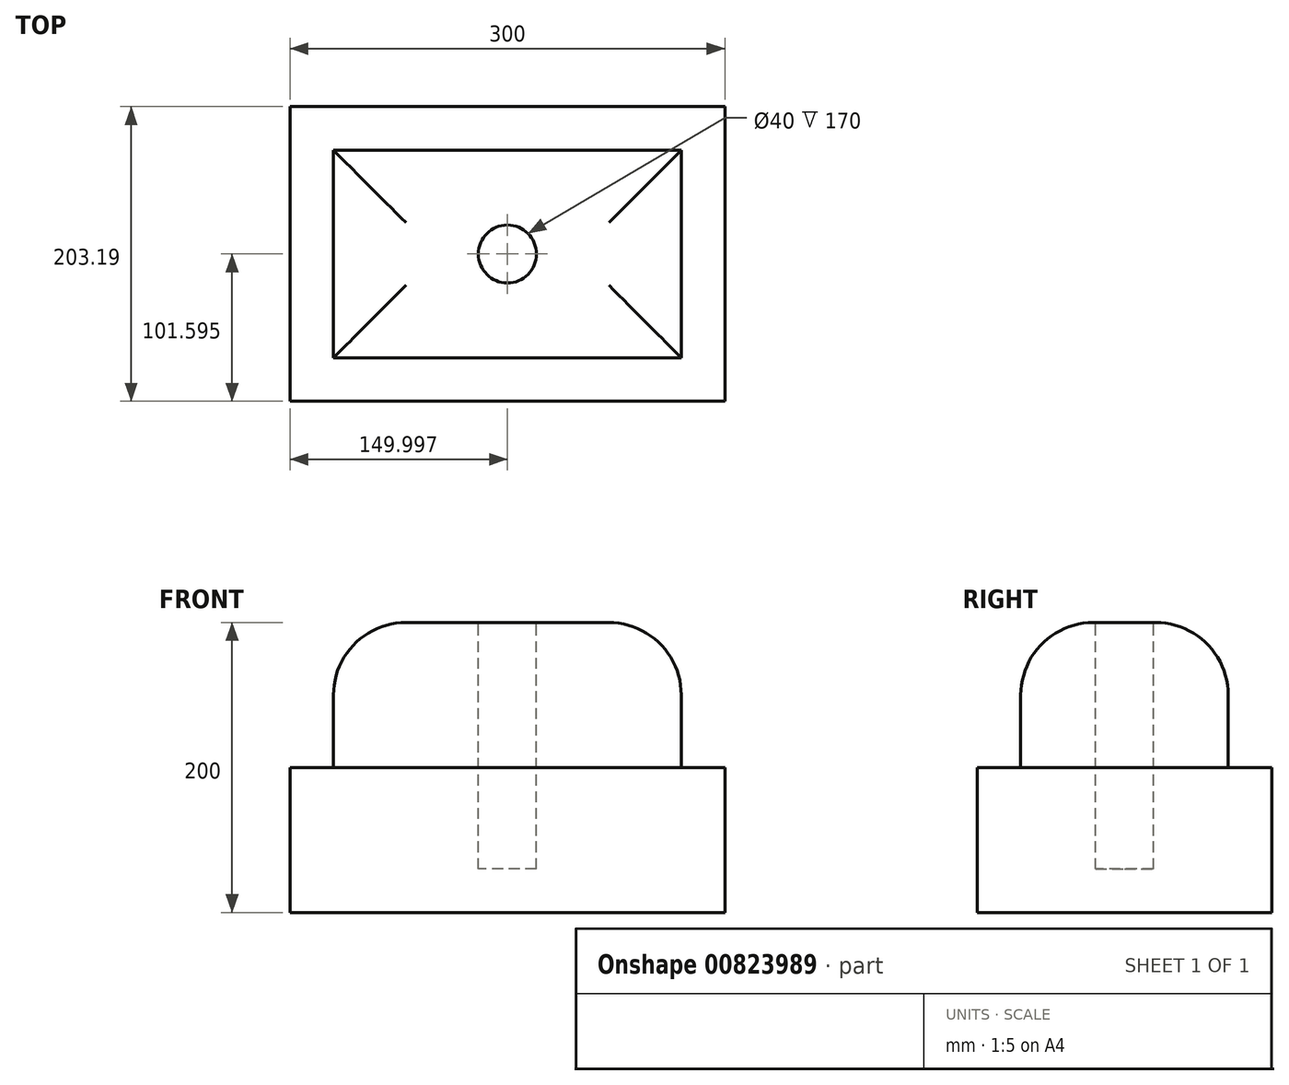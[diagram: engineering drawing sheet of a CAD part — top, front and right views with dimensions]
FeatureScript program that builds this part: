
annotation { "Feature Type Name" : "Feature", "Feature Type Description" : "" }
export const myFeature = defineFeature(function(context is Context, id is Id, definition is map)
    precondition{}
    {
        {
            var Q0;
            Q0=qCreatedBy(makeId("Top.planeOp"),FACE);
            var sketch = newSketch(context, id + "F0", { "sketchPlane" : qUnion([Q0])});
            skLineSegment(sketch, "E0", {"start": v(-72.68, 128.13) * mm, "end": v(227.32, 128.13) * mm});
            skLineSegment(sketch, "E1", {"start": v(-72.68, 128.13) * mm, "end": v(-72.68, -75.06) * mm});
            skLineSegment(sketch, "E2", {"start": v(-72.68, -75.06) * mm, "end": v(227.32, -75.06) * mm});
            skLineSegment(sketch, "E3", {"start": v(227.32, -75.06) * mm, "end": v(227.32, 128.13) * mm});
            skSolve(sketch);
        }
        {
            var Q0;
            Q0=makeQuery(id+"F0.imprint","IMPRINT",FACE,{"disambiguationData":[TD([[makeQuery(id+"F0.imprint","IMPRINT",EDGE,{"derivedFrom":sQuery(id+"F0.wireOp",EDGE,"E0")}),-1.0]])]});
            extrude(context, id + "F1", {"entities" : qUnion([Q0]), "depth" : 100 * mm, "offsetDistance" : 25 * mm});
        }
        {
            var Q0;
            Q0=makeQuery(id+"F1.opExtrude","CAP_FACE",FACE,{"disambiguationData":[OSD([sQuery(id+"F0.wireOp",EDGE,"E0"),sQuery(id+"F0.wireOp",EDGE,"E1"),sQuery(id+"F0.wireOp",EDGE,"E2"),sQuery(id+"F0.wireOp",EDGE,"E3")])],"isStart":false});
            var sketch = newSketch(context, id + "F2", { "sketchPlane" : qUnion([Q0])});
            skLineSegment(sketch, "E4", {"start": v(-42.68, 98.13) * mm, "end": v(197.32, 98.13) * mm});
            skLineSegment(sketch, "E5.MirrorCS", {"start": v(-42.68, -45.06) * mm, "end": v(197.32, -45.06) * mm});
            skLineSegment(sketch, "E6", {"start": v(-42.68, 98.13) * mm, "end": v(-42.68, -45.06) * mm});
            skLineSegment(sketch, "E7", {"start": v(197.32, 98.13) * mm, "end": v(197.32, -45.06) * mm});
            skSolve(sketch);
        }
        {
            var Q0;
            Q0 = qSketchRegion(id + "F2", true);
            extrude(context, id + "F3", {"entities" : qUnion([Q0]), "operationType" : NewBodyOperationType.ADD, "depth" : 100 * mm, "offsetDistance" : 25 * mm});
        }
        {
            var Q0;
            Q0=makeQuery(id+"F3.opExtrude","CAP_EDGE",EDGE,{"disambiguationData":[OSD([sQuery(id+"F2.wireOp",EDGE,"E4")])],"isStart":false});
            var Q1;
            Q1=makeQuery(id+"F3.opExtrude","CAP_EDGE",EDGE,{"disambiguationData":[OSD([sQuery(id+"F2.wireOp",EDGE,"E6")])],"isStart":false});
            var Q2;
            Q2=makeQuery(id+"F3.opExtrude","CAP_EDGE",EDGE,{"disambiguationData":[OSD([sQuery(id+"F2.wireOp",EDGE,"E5.MirrorCS")])],"isStart":false});
            var Q3;
            Q3=makeQuery(id+"F3.opExtrude","CAP_EDGE",EDGE,{"disambiguationData":[OSD([sQuery(id+"F2.wireOp",EDGE,"E7")])],"isStart":false});
            fillet(context, id + "F4", {"entities" : qUnion([Q0, Q1, Q2, Q3]), "radius" : 50 * mm, "tangentPropagation" : true, "allowEdgeOverflow" : false});
        }
        {
            var Q0;
            Q0=makeQuery(id+"F3.opExtrude","CAP_FACE",FACE,{"disambiguationData":[OSD([sQuery(id+"F2.wireOp",EDGE,"E4"),sQuery(id+"F2.wireOp",EDGE,"E5.MirrorCS"),sQuery(id+"F2.wireOp",EDGE,"E6"),sQuery(id+"F2.wireOp",EDGE,"E7")])],"isStart":false});
            var sketch = newSketch(context, id + "F5", { "sketchPlane" : qUnion([Q0])});
            skLineSegment(sketch, "E8", {"start": v(77.32, 48.13) * mm, "end": v(77.32, 4.94) * mm, "construction": true});
            skLineSegment(sketch, "E9", {"start": v(7.32, 26.54) * mm, "end": v(147.32, 26.54) * mm, "construction": true});
            skCircle(sketch, "E10", {"center": v(77.32, 26.54) * mm, "radius": 20 * mm});
            skSolve(sketch);
        }
        {
            var Q0;
            Q0=makeQuery(id+"F5.imprint","IMPRINT",FACE,{"disambiguationData":[TD([[makeQuery(id+"F5.imprint","IMPRINT",EDGE,{"derivedFrom":sQuery(id+"F5.wireOp",EDGE,"E10")}),1.0]])]});
            extrude(context, id + "F6", {"entities" : qUnion([Q0]), "operationType" : NewBodyOperationType.REMOVE, "oppositeDirection" : true, "depth" : 170 * mm, "offsetDistance" : 25 * mm});
        }
    });
